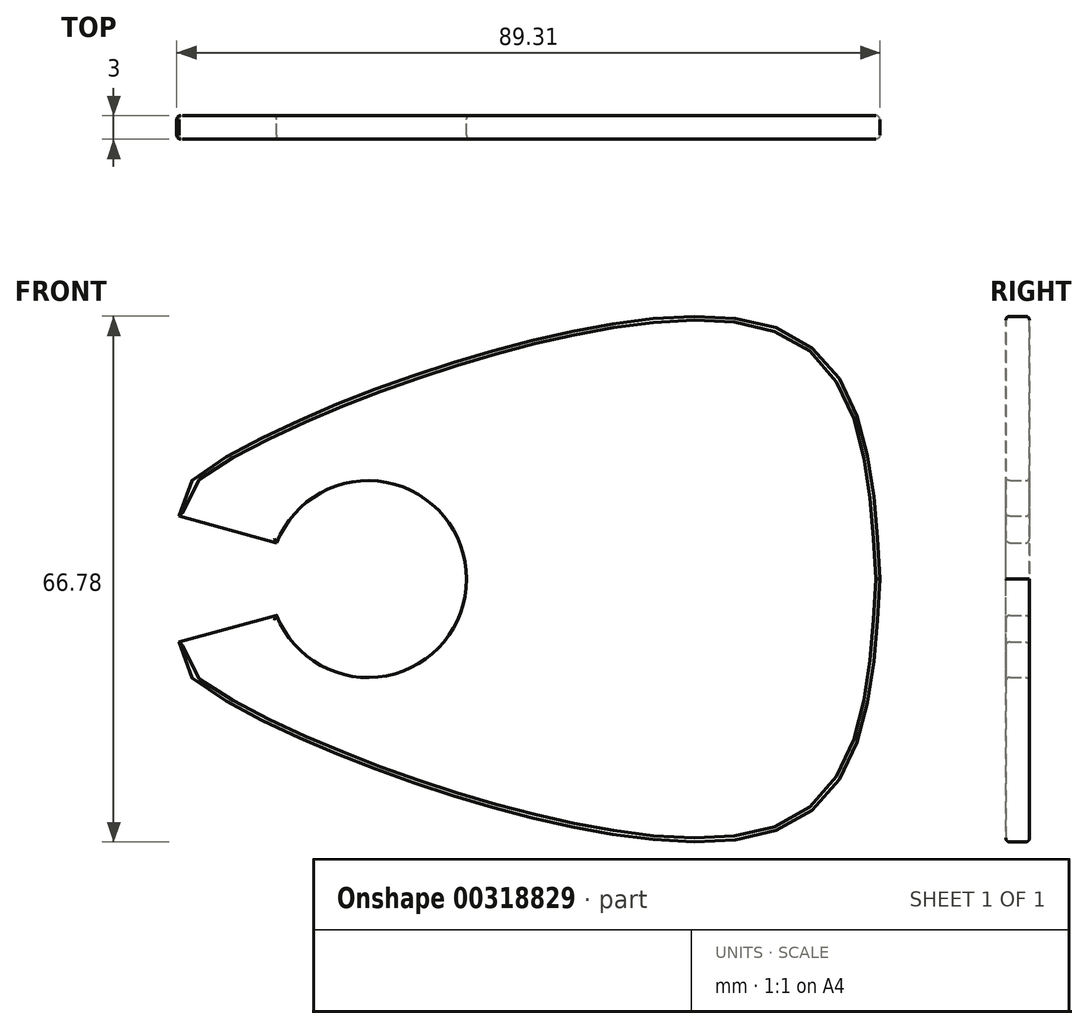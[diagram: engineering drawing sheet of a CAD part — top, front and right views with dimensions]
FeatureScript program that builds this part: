
annotation { "Feature Type Name" : "Feature", "Feature Type Description" : "" }
export const myFeature = defineFeature(function(context is Context, id is Id, definition is map)
    precondition{}
    {
        {
            var Q0;
            Q0=qCreatedBy(makeId("Front.planeOp"),FACE);
            var sketch = newSketch(context, id + "F0", { "sketchPlane" : qUnion([Q0])});
            skArc(sketch, "E0", {"start": v(12.5, 0) * mm, "mid": v(2.33, 12.28) * mm, "end": v(-11.63, 4.59) * mm});
            skLineSegment(sketch, "E1", {"start": v(-74.5, 0) * mm, "end": v(71.2, 0) * mm, "construction": true});
            skLineSegment(sketch, "E2", {"start": v(-24, 8) * mm, "end": v(-11.63, 4.59) * mm});
            skFitSpline(sketch, "E3", {"points": [v(-24, 8) * mm, v(-23, 12) * mm, v(50, 32.5) * mm, v(65, 0) * mm], "startDerivative": vector(-9.07, 28.1) * mm, "endDerivative": vector(6.8, -121.57) * mm});
            skFitSpline(sketch, "E4.MirrorCS", {"points": [v(-24, -8) * mm, v(-23, -12) * mm, v(50, -32.5) * mm, v(65, 0) * mm], "startDerivative": vector(-9.07, -28.1) * mm, "endDerivative": vector(6.8, 121.57) * mm});
            skArc(sketch, "E5.MirrorCS", {"start": v(12.5, 0) * mm, "mid": v(2.33, -12.28) * mm, "end": v(-11.63, -4.59) * mm});
            skLineSegment(sketch, "E6.MirrorCS", {"start": v(-24, -8) * mm, "end": v(-11.63, -4.59) * mm});
            skSolve(sketch);
        }
        {
            var Q0;
            Q0 = qSketchRegion(id + "F0", true);
            extrude(context, id + "F1", {"entities" : qUnion([Q0]), "depth" : 3 * mm});
        }
        {
            var Q0;
            Q0=makeQuery(id+"F1.opExtrude","CAP_FACE",FACE,{"disambiguationData":[OSD([sQuery(id+"F0.wireOp",EDGE,"E0"),sQuery(id+"F0.wireOp",EDGE,"E2"),sQuery(id+"F0.wireOp",EDGE,"E3"),sQuery(id+"F0.wireOp",EDGE,"E4.MirrorCS"),sQuery(id+"F0.wireOp",EDGE,"E5.MirrorCS"),sQuery(id+"F0.wireOp",EDGE,"E6.MirrorCS")])],"isStart":false});
            var Q1;
            Q1=makeQuery(id+"F1.opExtrude","CAP_FACE",FACE,{"disambiguationData":[OSD([sQuery(id+"F0.wireOp",EDGE,"E0"),sQuery(id+"F0.wireOp",EDGE,"E2"),sQuery(id+"F0.wireOp",EDGE,"E3"),sQuery(id+"F0.wireOp",EDGE,"E4.MirrorCS"),sQuery(id+"F0.wireOp",EDGE,"E5.MirrorCS"),sQuery(id+"F0.wireOp",EDGE,"E6.MirrorCS")])],"isStart":true});
            fillet(context, id + "F2", {"entities" : qUnion([Q0, Q1]), "radius" : 0.5 * mm, "tangentPropagation" : true, "allowEdgeOverflow" : false});
        }
    });
